# Revit family: Electrical-Teknion-YEFPW_Flush_Power_Module_WE_Connect-R2022
name_source: partatom
category: Furniture
units: mm (PartAtom-declared; Revit-internal decimal feet)

## family parameters
Always vertical = Yes
Cut with Voids When Loaded = No
Enable Cutting in Views = No
OmniClass Number = 23.40.20.00
OmniClass Title = General Furniture and Specialties
Render Appearance Source = Family Geometry
Room Calculation Point = No
Shared = Yes
Work Plane-Based = No

## types (3) — shared parameters
Assembly Code = E2020200
Faceplate Style = Only Pick One from Below
Manufacturer = Teknion
Manufacturer Fax = 416.661.4586
Part Number = YEFPW
Product Documentation Link = https://www.teknion.com
Product Line = Electrical
Product Page URL = https://www.teknion.com
R - Rectangular = No
Series = Power Accessories
Sustainability Data = https://www.teknion.com
URL = www.teknion.com
Unit Weight URL = http://www.teknion.com
Warranty = http://www.teknion.com
zero-valued in all types: Default Elevation

## per-type parameters (varying)
| type | 2D - T | C - Circular | Description | Model | T - Rectangular With Pass Through |
| Circular Faceplate | No | Yes | Flush Power Module, WE Connect, Circular Faceplate Style, Dual Electrical Cut Out | YEFPWCAH__ | No |
| Rectangular With Pass Through Faceplate | Yes | No | Flush Power Module, WE Connect, Rectangular With Pass Through Faceplate Style, Triple Electrical Cut Out | YEFPWTAJ__ | Yes |
| Rectangular Faceplate | Yes | No | Flush Power Module, WE Connect, Rectangular Faceplate Style | YEFPWR___ | Yes |

## geometry (parser evidence)
native form markers: Sweep x16
no freeform markers — native parametric forms only
